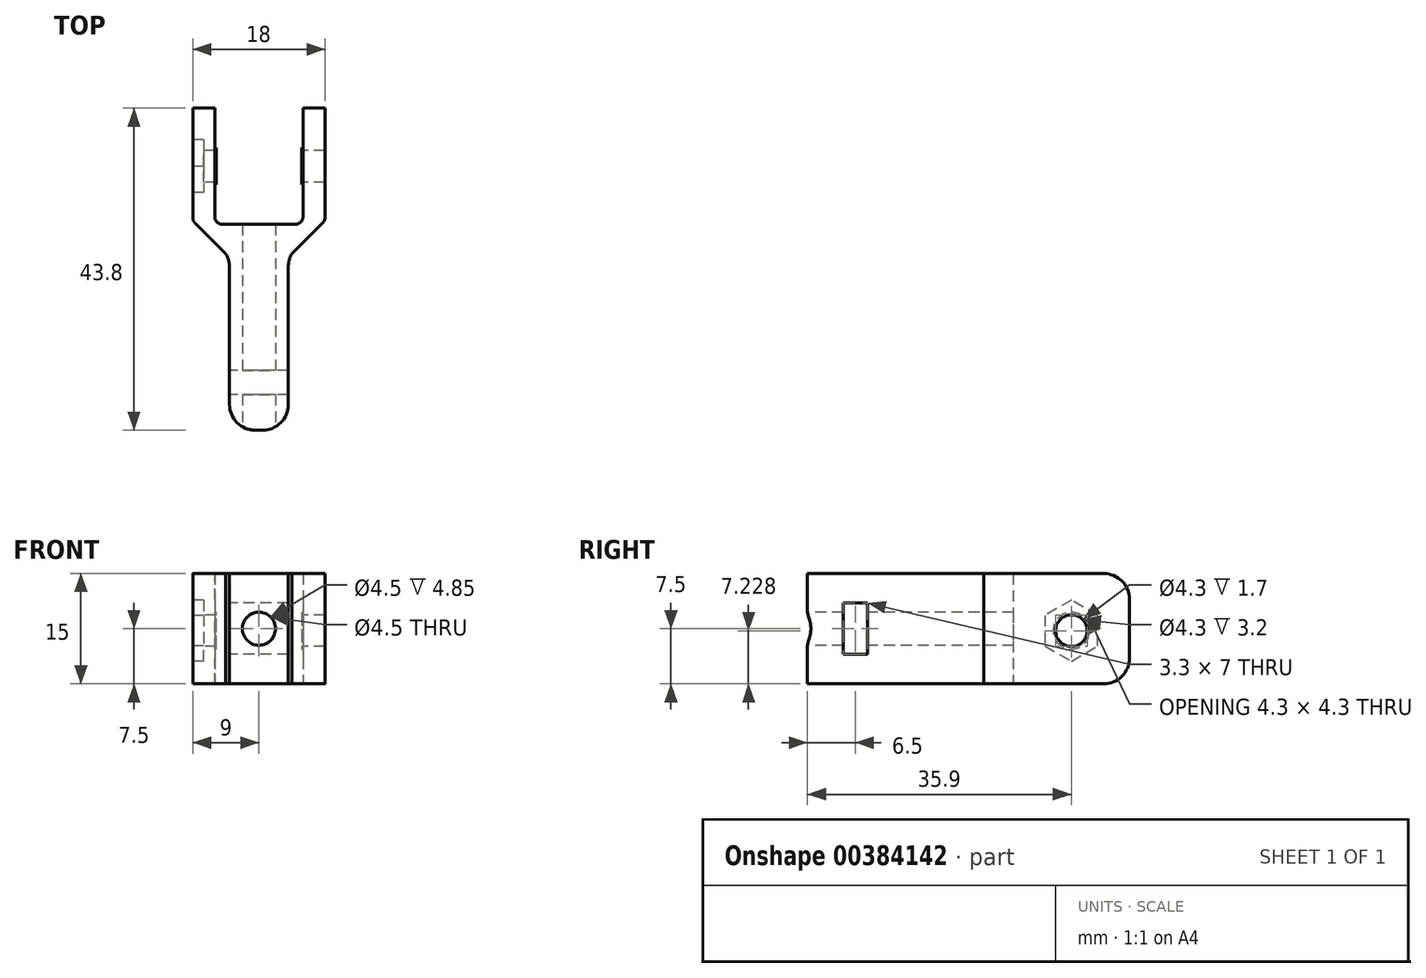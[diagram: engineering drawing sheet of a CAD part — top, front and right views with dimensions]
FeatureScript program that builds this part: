
annotation { "Feature Type Name" : "Feature", "Feature Type Description" : "" }
export const myFeature = defineFeature(function(context is Context, id is Id, definition is map)
    precondition{}
    {
        {
            var Q0;
            Q0=qCreatedBy(makeId("Top.planeOp"),FACE);
            var sketch = newSketch(context, id + "F0", { "sketchPlane" : qUnion([Q0])});
            skLineSegment(sketch, "E0", {"start": v(0, 0) * mm, "end": v(12, 0) * mm});
            skLineSegment(sketch, "E1", {"start": v(12, 0) * mm, "end": v(12, 15.8) * mm});
            skLineSegment(sketch, "E2", {"start": v(12, 15.8) * mm, "end": v(15, 15.8) * mm});
            skLineSegment(sketch, "E3", {"start": v(15, 15.8) * mm, "end": v(15, -4) * mm});
            skLineSegment(sketch, "E4", {"start": v(15, -4) * mm, "end": v(-3, -4) * mm});
            skLineSegment(sketch, "E5", {"start": v(-3, -4) * mm, "end": v(-3, 15.8) * mm});
            skLineSegment(sketch, "E6", {"start": v(-3, 15.8) * mm, "end": v(0, 15.8) * mm});
            skLineSegment(sketch, "E7", {"start": v(0, 15.8) * mm, "end": v(0, 0) * mm});
            skLineSegment(sketch, "E8", {"start": v(6, 0) * mm, "end": v(6, -31.45) * mm, "construction": true});
            skPoint(sketch, "E8.endSnap0", {"position": v(6, -4) * mm});
            skLineSegment(sketch, "E9", {"start": v(34.77, 15.8) * mm, "end": v(-22.08, 15.8) * mm, "construction": true});
            skLineSegment(sketch, "E10", {"start": v(6, -4) * mm, "end": v(2, -4) * mm});
            skLineSegment(sketch, "E11", {"start": v(2, -4) * mm, "end": v(2, -28) * mm});
            skLineSegment(sketch, "E12", {"start": v(2, -28) * mm, "end": v(10, -28) * mm});
            skLineSegment(sketch, "E13", {"start": v(10, -28) * mm, "end": v(10, -4) * mm});
            skSolve(sketch);
        }
        {
            var Q0;
            Q0=qSketchRegion(id+"F0",true);
            extrude(context, id + "F1", {"entities" : qUnion([Q0]), "depth" : 15 * mm});
        }
        {
            var Q0;
            Q0=makeQuery(id+"F1.opExtrude","SWEPT_FACE",FACE,{"disambiguationData":[OSD([sQuery(id+"F0.wireOp",EDGE,"E12")])]});
            var sketch = newSketch(context, id + "F2", { "sketchPlane" : qUnion([Q0])});
            skLineSegment(sketch, "E14", {"start": v(2, 7.5) * mm, "end": v(10, 7.5) * mm, "construction": true});
            skLineSegment(sketch, "E15", {"start": v(6, 15) * mm, "end": v(6, 0) * mm, "construction": true});
            skCircle(sketch, "E16", {"center": v(6, 7.5) * mm, "radius": 2.25 * mm});
            skSolve(sketch);
        }
        {
            var Q0;
            Q0=makeQuery(id+"F2.imprint","IMPRINT",FACE,{"disambiguationData":[TD([[makeQuery(id+"F2.imprint","IMPRINT",EDGE,{"derivedFrom":sQuery(id+"F2.wireOp",EDGE,"E16")}),1.0]])]});
            extrude(context, id + "F3", {"entities" : qUnion([Q0]), "operationType" : NewBodyOperationType.REMOVE, "endBound" : BoundingType.THROUGH_ALL, "oppositeDirection" : true, "depth" : 18 * mm});
        }
        {
            var Q0;
            Q0=makeQuery(id+"F1.opExtrude","SWEPT_FACE",FACE,{"disambiguationData":[OSD([sQuery(id+"F0.wireOp",EDGE,"E5")])]});
            var sketch = newSketch(context, id + "F4", { "sketchPlane" : qUnion([Q0])});
            skLineSegment(sketch, "E17", {"start": v(0, 15.46) * mm, "end": v(0, -1) * mm, "construction": true});
            skLineSegment(sketch, "E18", {"start": v(0, 7.23) * mm, "end": v(-15.8, 7.23) * mm, "construction": true});
            skLineSegment(sketch, "E19", {"start": v(-7.9, 7.23) * mm, "end": v(-7.9, 15) * mm, "construction": true});
            skLineSegment(sketch, "E20", {"start": v(-7.9, 15) * mm, "end": v(-7.9, 0) * mm, "construction": true});
            skCircle(sketch, "E21", {"center": v(-7.9, 7.23) * mm, "radius": 2.15 * mm});
            skCircle(sketch, "E22.cCircle", {"center": v(-7.9, 7.23) * mm, "radius": 3.6 * mm, "construction": true});
            skLineSegment(sketch, "E22.0", {"start": v(-4.3, 9.3) * mm, "end": v(-4.3, 5.15) * mm});
            skLineSegment(sketch, "E22.1", {"start": v(-4.3, 5.15) * mm, "end": v(-7.9, 3.07) * mm});
            skLineSegment(sketch, "E22.2", {"start": v(-7.9, 3.07) * mm, "end": v(-11.5, 5.15) * mm});
            skLineSegment(sketch, "E22.3", {"start": v(-11.5, 5.15) * mm, "end": v(-11.5, 9.3) * mm});
            skLineSegment(sketch, "E22.4", {"start": v(-11.5, 9.3) * mm, "end": v(-7.9, 11.38) * mm});
            skLineSegment(sketch, "E22.5", {"start": v(-7.9, 11.38) * mm, "end": v(-4.3, 9.3) * mm});
            skPoint(sketch, "E22.0.midPoint", {"position": v(-4.3, 7.23) * mm});
            skSolve(sketch);
        }
        {
            var Q0;
            Q0=makeQuery(id+"F4.imprint","IMPRINT",FACE,{"disambiguationData":[TD([[makeQuery(id+"F4.imprint","IMPRINT",EDGE,{"derivedFrom":sQuery(id+"F4.wireOp",EDGE,"E21")}),1.0]])]});
            extrude(context, id + "F5", {"entities" : qUnion([Q0]), "operationType" : NewBodyOperationType.REMOVE, "oppositeDirection" : true, "depth" : 25 * mm});
        }
        {
            var Q0;
            Q0=makeQuery(id+"F1.opExtrude","SWEPT_FACE",FACE,{"disambiguationData":[OSD([sQuery(id+"F0.wireOp",EDGE,"E11")])]});
            var sketch = newSketch(context, id + "F6", { "sketchPlane" : qUnion([Q0])});
            skLineSegment(sketch, "E23", {"start": v(21.5, 15) * mm, "end": v(21.5, 0) * mm, "construction": true});
            skLineSegment(sketch, "E24", {"start": v(28, 7.5) * mm, "end": v(4, 7.5) * mm, "construction": true});
            skLineSegment(sketch, "E25.bottom", {"start": v(23.15, 11) * mm, "end": v(19.85, 11) * mm});
            skLineSegment(sketch, "E25.top", {"start": v(23.15, 4) * mm, "end": v(19.85, 4) * mm});
            skLineSegment(sketch, "E25.left", {"start": v(23.15, 11) * mm, "end": v(23.15, 4) * mm});
            skLineSegment(sketch, "E25.right", {"start": v(19.85, 11) * mm, "end": v(19.85, 4) * mm});
            skPoint(sketch, "E25.middle", {"position": v(21.5, 7.5) * mm});
            skSolve(sketch);
        }
        {
            var Q0;
            Q0=makeQuery(id+"F6.imprint","IMPRINT",FACE,{"disambiguationData":[TD([[makeQuery(id+"F6.imprint","IMPRINT",EDGE,{"derivedFrom":sQuery(id+"F6.wireOp",EDGE,"E25.bottom")}),1.0]])]});
            extrude(context, id + "F7", {"entities" : qUnion([Q0]), "operationType" : NewBodyOperationType.REMOVE, "oppositeDirection" : true, "depth" : 25 * mm});
        }
        {
            var Q0;
            Q0=makeQuery(id+"F4.imprint","IMPRINT",FACE,{"disambiguationData":[TD([[makeQuery(id+"F4.imprint","IMPRINT",EDGE,{"derivedFrom":sQuery(id+"F4.wireOp",EDGE,"E21")}),-1.0]])]});
            extrude(context, id + "F8", {"entities" : qUnion([Q0]), "operationType" : NewBodyOperationType.REMOVE, "oppositeDirection" : true, "depth" : 1.5 * mm});
        }
        {
            var Q0;
            Q0=makeQuery(id+"F1.opExtrude","SWEPT_EDGE",EDGE,{"disambiguationData":[OSD([sQuery(id+"F0.wireOp",EDGE,"E4"),sQuery(id+"F0.wireOp",EDGE,"E5")])]});
            var Q1;
            Q1=makeQuery(id+"F1.opExtrude","SWEPT_EDGE",EDGE,{"disambiguationData":[OSD([sQuery(id+"F0.wireOp",EDGE,"E3"),sQuery(id+"F0.wireOp",EDGE,"E4")])]});
            chamfer(context, id + "F9", {"entities" : qUnion([Q0, Q1]), "width" : 4.5 * mm, "tangentPropagation" : true});
        }
        {
            var Q0;
            Q0=makeQuery(id+"F1.opExtrude","SWEPT_EDGE",EDGE,{"disambiguationData":[OSD([sQuery(id+"F0.wireOp",EDGE,"E4"),sQuery(id+"F0.wireOp",EDGE,"E13")])]});
            var Q1;
            Q1=makeQuery(id+"F1.opExtrude","SWEPT_EDGE",EDGE,{"disambiguationData":[OSD([sQuery(id+"F0.wireOp",EDGE,"E4"),sQuery(id+"F0.wireOp",EDGE,"E10"),sQuery(id+"F0.wireOp",EDGE,"E11")])]});
            var Q2;
            Q2=makeQuery(id+"F1.opExtrude","SWEPT_EDGE",EDGE,{"disambiguationData":[OSD([sQuery(id+"F0.wireOp",EDGE,"E12"),sQuery(id+"F0.wireOp",EDGE,"E13")])]});
            var Q3;
            Q3=makeQuery(id+"F1.opExtrude","SWEPT_EDGE",EDGE,{"disambiguationData":[OSD([sQuery(id+"F0.wireOp",EDGE,"E11"),sQuery(id+"F0.wireOp",EDGE,"E12")])]});
            var Q4;
            Q4=makeQuery(id+"F1.opExtrude","CAP_EDGE",EDGE,{"disambiguationData":[OSD([sQuery(id+"F0.wireOp",EDGE,"E6")])],"isStart":true});
            var Q5;
            Q5=makeQuery(id+"F1.opExtrude","CAP_EDGE",EDGE,{"disambiguationData":[OSD([sQuery(id+"F0.wireOp",EDGE,"E2")])],"isStart":true});
            var Q6;
            Q6=makeQuery(id+"F1.opExtrude","CAP_EDGE",EDGE,{"disambiguationData":[OSD([sQuery(id+"F0.wireOp",EDGE,"E2")])],"isStart":false});
            var Q7;
            Q7=makeQuery(id+"F1.opExtrude","CAP_EDGE",EDGE,{"disambiguationData":[OSD([sQuery(id+"F0.wireOp",EDGE,"E6")])],"isStart":false});
            fillet(context, id + "F10", {"entities" : qUnion([Q0, Q1, Q2, Q3, Q4, Q5, Q6, Q7]), "radius" : 3.5 * mm, "tangentPropagation" : true, "allowEdgeOverflow" : false});
        }
        {
            var Q0;
            Q0=makeQuery(id+"F1.opExtrude","SWEPT_EDGE",EDGE,{"disambiguationData":[OSD([sQuery(id+"F0.wireOp",EDGE,"E0"),sQuery(id+"F0.wireOp",EDGE,"E7")])]});
            var Q1;
            Q1=makeQuery(id+"F1.opExtrude","SWEPT_EDGE",EDGE,{"disambiguationData":[OSD([sQuery(id+"F0.wireOp",EDGE,"E0"),sQuery(id+"F0.wireOp",EDGE,"E1")])]});
            var Q2;
            {var subQ0=sQuery(id+"F0.wireOp",EDGE,"E3");Q2=makeQuery(id+"F9.opChamfer","BLEND_EDGE",EDGE,{"blendedFrom":[makeQuery(id+"F1.opExtrude","SWEPT_EDGE",EDGE,{"disambiguationData":[OSD([subQ0,sQuery(id+"F0.wireOp",EDGE,"E4")])]}),makeQuery(id+"F1.opExtrude","SWEPT_FACE",FACE,{"disambiguationData":[OSD([subQ0])]})],"blendedInto":[makeQuery(id+"F1.opExtrude","SWEPT_FACE",FACE,{"disambiguationData":[OSD([subQ0])]})]});}
            var Q3;
            {var subQ0=sQuery(id+"F0.wireOp",EDGE,"E5");Q3=makeQuery(id+"F9.opChamfer","BLEND_EDGE",EDGE,{"blendedFrom":[makeQuery(id+"F1.opExtrude","SWEPT_EDGE",EDGE,{"disambiguationData":[OSD([sQuery(id+"F0.wireOp",EDGE,"E4"),subQ0])]}),makeQuery(id+"F1.opExtrude","SWEPT_FACE",FACE,{"disambiguationData":[OSD([subQ0])]})],"blendedInto":[makeQuery(id+"F1.opExtrude","SWEPT_FACE",FACE,{"disambiguationData":[OSD([subQ0])]})]});}
            fillet(context, id + "F11", {"entities" : qUnion([Q0, Q1, Q2, Q3]), "radius" : 1 * mm, "tangentPropagation" : true, "allowEdgeOverflow" : false});
        }
        {
            var Q0;
            Q0=makeQuery(id+"F1.opExtrude","SWEPT_FACE",FACE,{"disambiguationData":[OSD([sQuery(id+"F0.wireOp",EDGE,"E1")])]});
            var sketch = newSketch(context, id + "F12", { "sketchPlane" : qUnion([Q0])});
            skCircle(sketch, "E26", {"center": v(-7.9, 7.23) * mm, "radius": 2.5 * mm});
            skSolve(sketch);
        }
        {
            var Q0;
            Q0=makeQuery(id+"F12.imprint","IMPRINT",FACE,{"disambiguationData":[TD([[makeQuery(id+"F12.imprint","IMPRINT",EDGE,{"derivedFrom":sQuery(id+"F12.wireOp",EDGE,"E26")}),1.0]])]});
            extrude(context, id + "F13", {"entities" : qUnion([Q0]), "operationType" : NewBodyOperationType.ADD, "depth" : .2 * mm});
        }
        {
            var Q0;
            Q0=makeQuery(id+"F1.opExtrude","SWEPT_FACE",FACE,{"disambiguationData":[OSD([sQuery(id+"F0.wireOp",EDGE,"E7")])]});
            var sketch = newSketch(context, id + "F14", { "sketchPlane" : qUnion([Q0])});
            skCircle(sketch, "E27", {"center": v(7.9, 7.23) * mm, "radius": 2.5 * mm});
            skSolve(sketch);
        }
        {
            var Q0;
            Q0=makeQuery(id+"F14.imprint","IMPRINT",FACE,{"disambiguationData":[TD([[makeQuery(id+"F14.imprint","IMPRINT",EDGE,{"derivedFrom":sQuery(id+"F14.wireOp",EDGE,"E27")}),1.0]])]});
            extrude(context, id + "F15", {"entities" : qUnion([Q0]), "operationType" : NewBodyOperationType.ADD, "depth" : .2 * mm});
        }
    });
